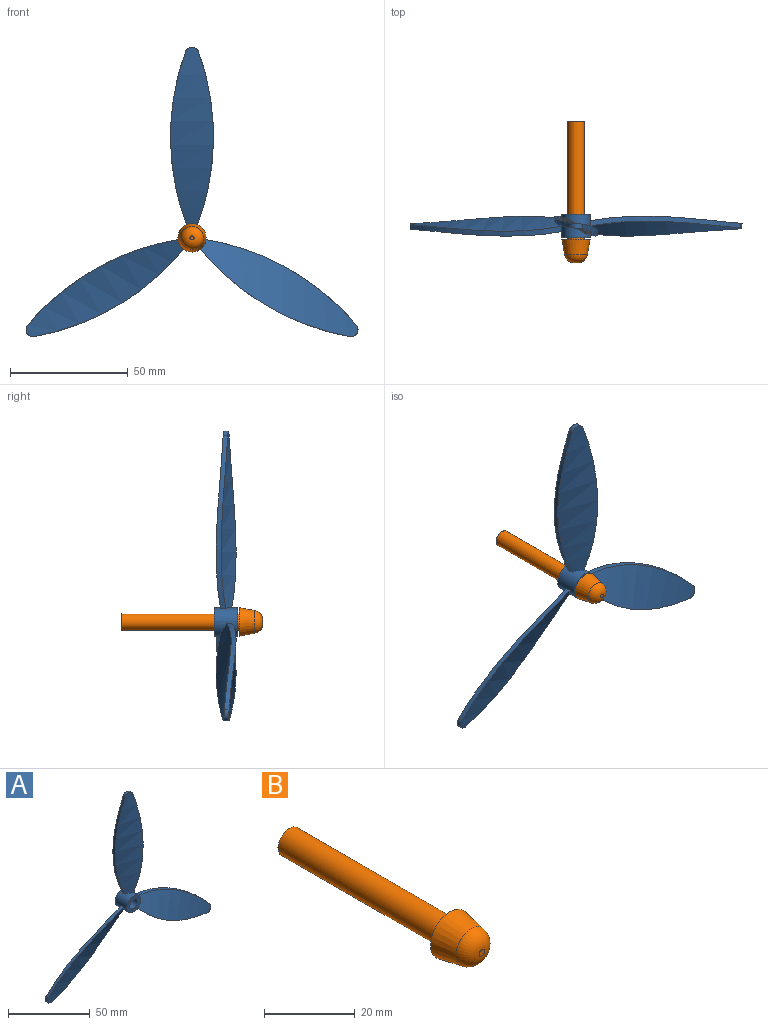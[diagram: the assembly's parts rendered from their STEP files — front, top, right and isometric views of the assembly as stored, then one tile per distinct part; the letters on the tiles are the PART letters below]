
ASSEMBLY  parts=2 mates=1
PART A: 19 faces, bbox 188.2x16.7x163 mm
  f0: cylinder r=106mm len=73.47mm, axis (0,1,0), area 154.2mm2, adj f2,f3,f4,f15
  f1: cylinder r=106mm len=73.47mm, axis (0,1,0), area 154.2mm2, adj f2,f3,f4,f15
  f2: bspline ~100x30mm, area 1083.3mm2, adj f0,f1,f4,f15
  f3: bspline ~100x30mm, area 1083.3mm2, adj f0,f1,f4,f15
  f4: cylinder r=3mm len=5.64mm, axis (0,1,0), area 14.4mm2, adj f0,f1,f2,f3
  f5: cylinder r=106mm len=63.35mm, axis (0,1,0), area 154.2mm2, adj f7,f8,f9,f15
  f6: cylinder r=106mm len=63.9mm, axis (0,1,0), area 154.2mm2, adj f7,f8,f9,f15
  f7: bspline ~100.85x73.81mm, area 1083.3mm2, adj f5,f6,f9,f15
  f8: bspline ~100.35x74.67mm, area 1083.3mm2, adj f5,f6,f9,f15
  f9: cylinder r=3mm len=4.93mm, axis (0,1,0), area 14.4mm2, adj f5,f6,f7,f8
  f10: cylinder r=106mm len=63.9mm, axis (0,1,0), area 154.2mm2, adj f12,f13,f14,f15
  f11: cylinder r=106mm len=63.35mm, axis (0,1,0), area 154.2mm2, adj f12,f13,f14,f15
  f12: bspline ~100.35x74.67mm, area 1083.3mm2, adj f10,f11,f14,f15
  f13: bspline ~100.85x73.81mm, area 1083.3mm2, adj f10,f11,f14,f15
  f14: cylinder r=3mm len=4.93mm, axis (0,1,0), area 14.4mm2, adj f10,f11,f12,f13
  f15: cylinder r=6mm len=12mm, axis (0,1,0), area 345.3mm2, adj f0,f1,f2,f3,f5,f6,f7,f8
  f16: plane 12x12mm, normal (0,-1,0), area 74.6mm2, adj f15,f18
  f17: plane 12x12mm, normal (0,1,0), area 74.6mm2, adj f15,f18
  f18: cylinder r=3.5mm len=10mm, axis (0,-1,0), area 219.9mm2, adj f16,f17
PART B: 6 faces, bbox 12x60x12 mm
  f0: cylinder r=3.5mm len=50mm, axis (0,1,0), area 1099.6mm2, adj f1,f4
  f1: plane 7x7mm, normal (0,1,0), area 38.5mm2, adj f0
  f2: cone r=6mm half-angle=10deg, axis (0,1,0), area 231.1mm2, adj f4,f5
  f3: plane 1.76x1.76mm, normal (0,-1,0), area 2.4mm2, adj f5
  f4: plane 12x12mm, normal (0,1,0), area 74.6mm2, adj f0,f2
  f5: torus R=0.88mm, axis (0,-1,0), area 114mm2, adj f2,f3
PLACE A t=(0,-44.5,0)mm
PLACE B at identity
MATE revolute A.f18 <-> B.f0  axis (0,-1,0) through (0,-49.5,0)mm
